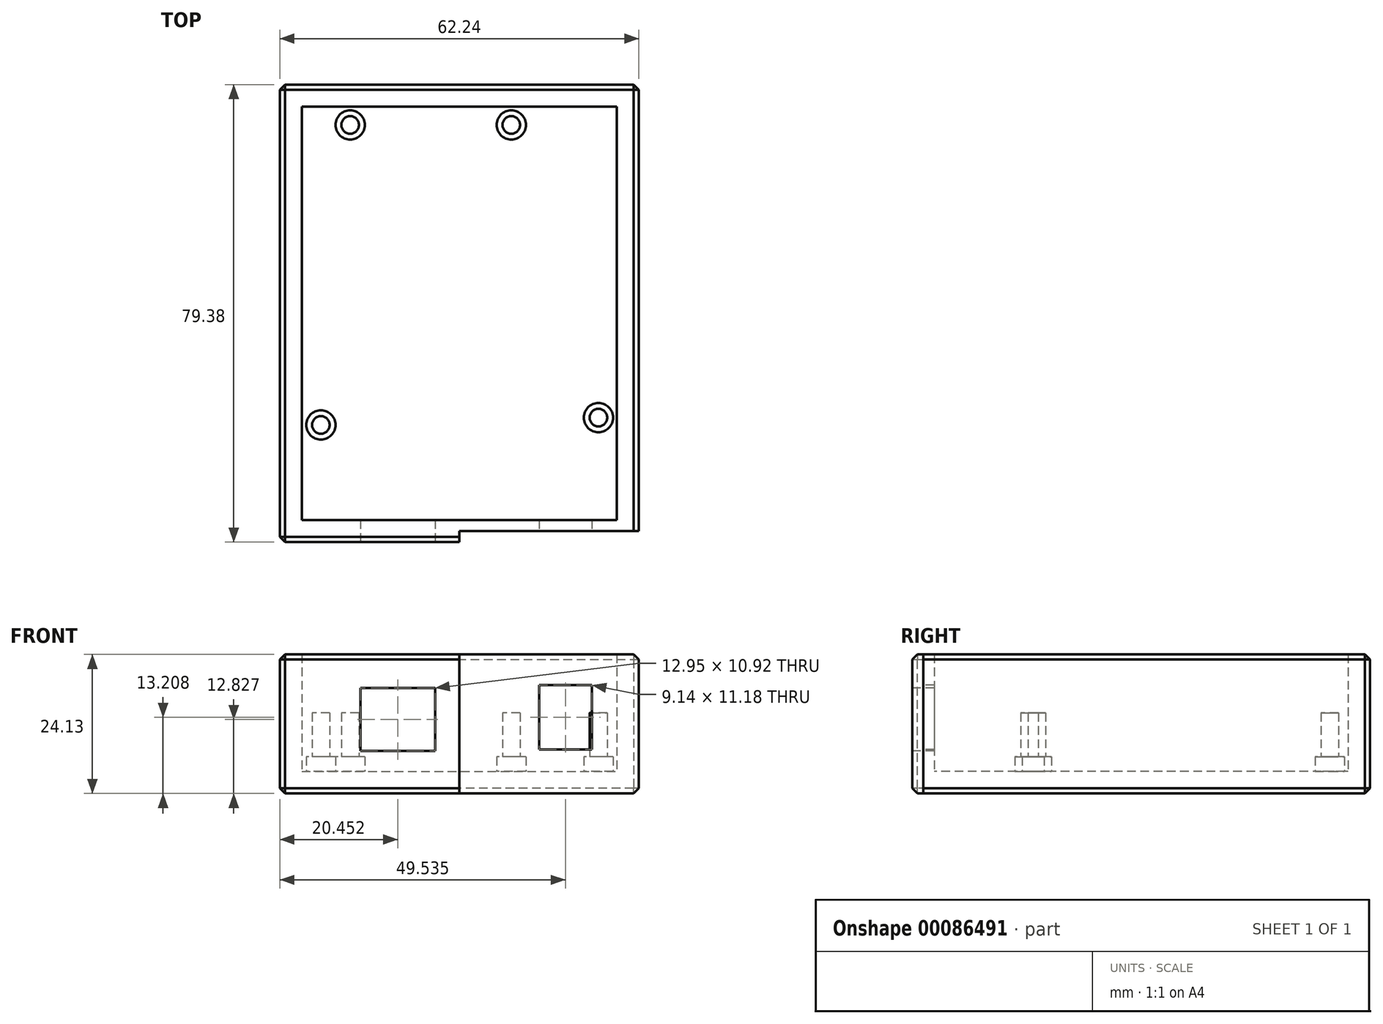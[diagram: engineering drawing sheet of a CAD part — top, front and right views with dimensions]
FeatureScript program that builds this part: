
annotation { "Feature Type Name" : "Feature", "Feature Type Description" : "" }
export const myFeature = defineFeature(function(context is Context, id is Id, definition is map)
    precondition{}
    {
        {
            var Q0;
            Q0=qCreatedBy(makeId("Top.planeOp"),FACE);
            var sketch = newSketch(context, id + "F0", { "sketchPlane" : qUnion([Q0])});
            skLineSegment(sketch, "E0.bottom", {"start": v(-31.11, 39.69) * mm, "end": v(31.12, 39.69) * mm});
            skLineSegment(sketch, "E0.top", {"start": v(-31.12, -39.69) * mm, "end": v(31.11, -39.69) * mm});
            skLineSegment(sketch, "E0.left", {"start": v(-31.11, 39.69) * mm, "end": v(-31.12, -39.69) * mm});
            skLineSegment(sketch, "E0.right", {"start": v(31.12, 39.69) * mm, "end": v(31.11, -39.69) * mm});
            skPoint(sketch, "E0.middle", {"position": v(0, 0) * mm});
            skSolve(sketch);
        }
        {
            var Q0;
            Q0 = qSketchRegion(id + "F0", true);
            extrude(context, id + "F1", {"entities" : qUnion([Q0]), "depth" : 24.13 * mm});
        }
        {
            var Q0;
            Q0=makeQuery(id+"F1.opExtrude","CAP_FACE",FACE,{"disambiguationData":[OSD([sQuery(id+"F0.wireOp",EDGE,"E0.bottom"),sQuery(id+"F0.wireOp",EDGE,"E0.top"),sQuery(id+"F0.wireOp",EDGE,"E0.left"),sQuery(id+"F0.wireOp",EDGE,"E0.right")])],"isStart":false});
            shell(context, id + "F2", {"entities" : qUnion([Q0]), "thickness" : 3.8 * mm});
        }
        {
            var Q0;
            Q0=makeQuery(id+"F2.opShell","OFFSET_FACE",FACE,{"disambiguationData":[OSD([sQuery(id+"F0.wireOp",EDGE,"E0.bottom"),sQuery(id+"F0.wireOp",EDGE,"E0.top"),sQuery(id+"F0.wireOp",EDGE,"E0.left"),sQuery(id+"F0.wireOp",EDGE,"E0.right")])]});
            var sketch = newSketch(context, id + "F3", { "sketchPlane" : qUnion([Q0])});
            skCircle(sketch, "E1", {"center": v(9.02, 32.7) * mm, "radius": 2.54 * mm});
            skSolve(sketch);
        }
        {
            var Q0;
            Q0=makeQuery(id+"F2.opShell","OFFSET_FACE",FACE,{"disambiguationData":[OSD([sQuery(id+"F0.wireOp",EDGE,"E0.bottom"),sQuery(id+"F0.wireOp",EDGE,"E0.top"),sQuery(id+"F0.wireOp",EDGE,"E0.left"),sQuery(id+"F0.wireOp",EDGE,"E0.right")])]});
            var sketch = newSketch(context, id + "F4", { "sketchPlane" : qUnion([Q0])});
            skCircle(sketch, "E2", {"center": v(9.02, 32.7) * mm, "radius": 2.54 * mm});
            skCircle(sketch, "E3", {"center": v(-18.92, 32.7) * mm, "radius": 2.54 * mm});
            skCircle(sketch, "E4", {"center": v(-24, -19.37) * mm, "radius": 2.54 * mm});
            skCircle(sketch, "E5", {"center": v(24.13, -18.1) * mm, "radius": 2.54 * mm});
            skSolve(sketch);
        }
        {
            var Q0;
            Q0 = qSketchRegion(id + "F4", true);
            extrude(context, id + "F5", {"entities" : qUnion([Q0]), "operationType" : NewBodyOperationType.ADD, "depth" : 2.54 * mm});
        }
        {
            var Q0;
            Q0=makeQuery(id+"F5.opExtrude","CAP_FACE",FACE,{"disambiguationData":[OSD([sQuery(id+"F4.wireOp",EDGE,"E3")])],"isStart":false});
            cPlane(context, id + "F6", {"entities" : qUnion([Q0]), "cplaneType" : CPlaneType.OFFSET, "offset" : 0 * mm, "width" : 152.4 * mm, "height" : 152.4 * mm});
        }
        {
            var Q0;
            Q0=qCreatedBy(id+"F6.planeOp",FACE);
            var sketch = newSketch(context, id + "F7", { "sketchPlane" : qUnion([Q0])});
            skCircle(sketch, "E6", {"center": v(9.02, 32.7) * mm, "radius": 1.52 * mm});
            skCircle(sketch, "E7", {"center": v(-18.92, 32.7) * mm, "radius": 1.52 * mm});
            skCircle(sketch, "E8", {"center": v(-24, -19.37) * mm, "radius": 1.52 * mm});
            skCircle(sketch, "E9", {"center": v(24.13, -18.1) * mm, "radius": 1.52 * mm});
            skSolve(sketch);
        }
        {
            var Q0;
            Q0 = qSketchRegion(id + "F7", true);
            extrude(context, id + "F8", {"entities" : qUnion([Q0]), "operationType" : NewBodyOperationType.ADD, "depth" : 7.62 * mm});
        }
        {
            var Q0;
            Q0=makeQuery(id+"F1.opExtrude","SWEPT_FACE",FACE,{"disambiguationData":[OSD([sQuery(id+"F0.wireOp",EDGE,"E0.top")])]});
            var sketch = newSketch(context, id + "F9", { "sketchPlane" : qUnion([Q0])});
            skLineSegment(sketch, "E10.bottom", {"start": v(-17.15, 18.29) * mm, "end": v(-4.2, 18.29) * mm});
            skLineSegment(sketch, "E10.top", {"start": v(-17.15, 7.37) * mm, "end": v(-4.2, 7.37) * mm});
            skLineSegment(sketch, "E10.left", {"start": v(-17.15, 18.29) * mm, "end": v(-17.15, 7.37) * mm});
            skLineSegment(sketch, "E10.right", {"start": v(-4.2, 18.29) * mm, "end": v(-4.2, 7.37) * mm});
            skLineSegment(sketch, "E11.bottom", {"start": v(13.84, 18.8) * mm, "end": v(22.99, 18.8) * mm});
            skLineSegment(sketch, "E11.top", {"start": v(13.84, 7.62) * mm, "end": v(22.99, 7.62) * mm});
            skLineSegment(sketch, "E11.left", {"start": v(13.84, 18.8) * mm, "end": v(13.84, 7.62) * mm});
            skLineSegment(sketch, "E11.right", {"start": v(22.99, 18.8) * mm, "end": v(22.99, 7.62) * mm});
            skSolve(sketch);
        }
        {
            var Q0;
            Q0 = qSketchRegion(id + "F9", true);
            var Q1;
            Q1=makeQuery(id+"F2.opShell","OFFSET_FACE",FACE,{"disambiguationData":[OSD([sQuery(id+"F0.wireOp",EDGE,"E0.top")])]});
            extrude(context, id + "F10", {"entities" : qUnion([Q0]), "operationType" : NewBodyOperationType.REMOVE, "endBound" : BoundingType.UP_TO_SURFACE, "oppositeDirection" : true, "endBoundEntityFace" : qUnion([Q1]), "depth" : 25.4 * mm});
        }
        {
            var Q0;
            Q0=makeQuery(id+"F1.opExtrude","SWEPT_FACE",FACE,{"disambiguationData":[OSD([sQuery(id+"F0.wireOp",EDGE,"E0.top")])]});
            var sketch = newSketch(context, id + "F11", { "sketchPlane" : qUnion([Q0])});
            skLineSegment(sketch, "E12.bottom", {"start": v(31.11, 24.13) * mm, "end": v(0, 24.13) * mm});
            skLineSegment(sketch, "E12.top", {"start": v(31.11, 0) * mm, "end": v(0, 0) * mm});
            skLineSegment(sketch, "E12.left", {"start": v(31.11, 24.13) * mm, "end": v(31.11, 0) * mm});
            skLineSegment(sketch, "E12.right", {"start": v(0, 24.13) * mm, "end": v(0, 0) * mm});
            skSolve(sketch);
        }
        {
            var Q0;
            Q0 = qSketchRegion(id + "F11", true);
            extrude(context, id + "F12", {"entities" : qUnion([Q0]), "operationType" : NewBodyOperationType.REMOVE, "oppositeDirection" : true, "depth" : 1.9 * mm});
        }
        {
            var Q0;
            Q0=makeQuery(id+"F1.opExtrude","CAP_EDGE",EDGE,{"disambiguationData":[OSD([sQuery(id+"F0.wireOp",EDGE,"E0.top")])],"isStart":false});
            var Q1;
            Q1=makeQuery(id+"F1.opExtrude","CAP_EDGE",EDGE,{"disambiguationData":[OSD([sQuery(id+"F0.wireOp",EDGE,"E0.left")])],"isStart":false});
            var Q2;
            Q2=makeQuery(id+"F1.opExtrude","CAP_EDGE",EDGE,{"disambiguationData":[OSD([sQuery(id+"F0.wireOp",EDGE,"E0.bottom")])],"isStart":false});
            var Q3;
            Q3=makeQuery(id+"F1.opExtrude","SWEPT_EDGE",EDGE,{"disambiguationData":[OSD([sQuery(id+"F0.wireOp",EDGE,"E0.bottom"),sQuery(id+"F0.wireOp",EDGE,"E0.right")])]});
            var Q4;
            Q4=makeQuery(id+"F1.opExtrude","CAP_EDGE",EDGE,{"disambiguationData":[OSD([sQuery(id+"F0.wireOp",EDGE,"E0.right")])],"isStart":false});
            var Q5;
            Q5=makeQuery(id+"F12.boolean.opBoolean","COPY",EDGE,{"derivedFrom":makeQuery(id+"F12.opExtrude","CAP_EDGE",EDGE,{"disambiguationData":[OSD([sQuery(id+"F11.wireOp",EDGE,"E12.left")])],"isStart":false})});
            var Q6;
            Q6=makeQuery(id+"F1.opExtrude","CAP_EDGE",EDGE,{"disambiguationData":[OSD([sQuery(id+"F0.wireOp",EDGE,"E0.right")])],"isStart":true});
            var Q7;
            Q7=makeQuery(id+"F12.boolean.opBoolean","COPY",EDGE,{"derivedFrom":makeQuery(id+"F12.opExtrude","CAP_EDGE",EDGE,{"disambiguationData":[OSD([sQuery(id+"F11.wireOp",EDGE,"E12.top")])],"isStart":false})});
            var Q8;
            Q8=makeQuery(id+"F12.boolean.opBoolean","COPY",EDGE,{"derivedFrom":makeQuery(id+"F12.opExtrude","CAP_EDGE",EDGE,{"disambiguationData":[OSD([sQuery(id+"F11.wireOp",EDGE,"E12.right")])],"isStart":true})});
            var Q9;
            Q9=makeQuery(id+"F1.opExtrude","CAP_EDGE",EDGE,{"disambiguationData":[OSD([sQuery(id+"F0.wireOp",EDGE,"E0.top")])],"isStart":true});
            var Q10;
            Q10=makeQuery(id+"F1.opExtrude","SWEPT_EDGE",EDGE,{"disambiguationData":[OSD([sQuery(id+"F0.wireOp",EDGE,"E0.top"),sQuery(id+"F0.wireOp",EDGE,"E0.left")])]});
            var Q11;
            Q11=makeQuery(id+"F1.opExtrude","SWEPT_EDGE",EDGE,{"disambiguationData":[OSD([sQuery(id+"F0.wireOp",EDGE,"E0.bottom"),sQuery(id+"F0.wireOp",EDGE,"E0.left")])]});
            var Q12;
            Q12=makeQuery(id+"F1.opExtrude","CAP_EDGE",EDGE,{"disambiguationData":[OSD([sQuery(id+"F0.wireOp",EDGE,"E0.left")])],"isStart":true});
            var Q13;
            Q13=makeQuery(id+"F1.opExtrude","CAP_EDGE",EDGE,{"disambiguationData":[OSD([sQuery(id+"F0.wireOp",EDGE,"E0.bottom")])],"isStart":true});
            chamfer(context, id + "F13", {"entities" : qUnion([Q0, Q1, Q2, Q3, Q4, Q5, Q6, Q7, Q8, Q9, Q10, Q11, Q12, Q13]), "width" : 0.89 * mm, "tangentPropagation" : true});
        }
    });
